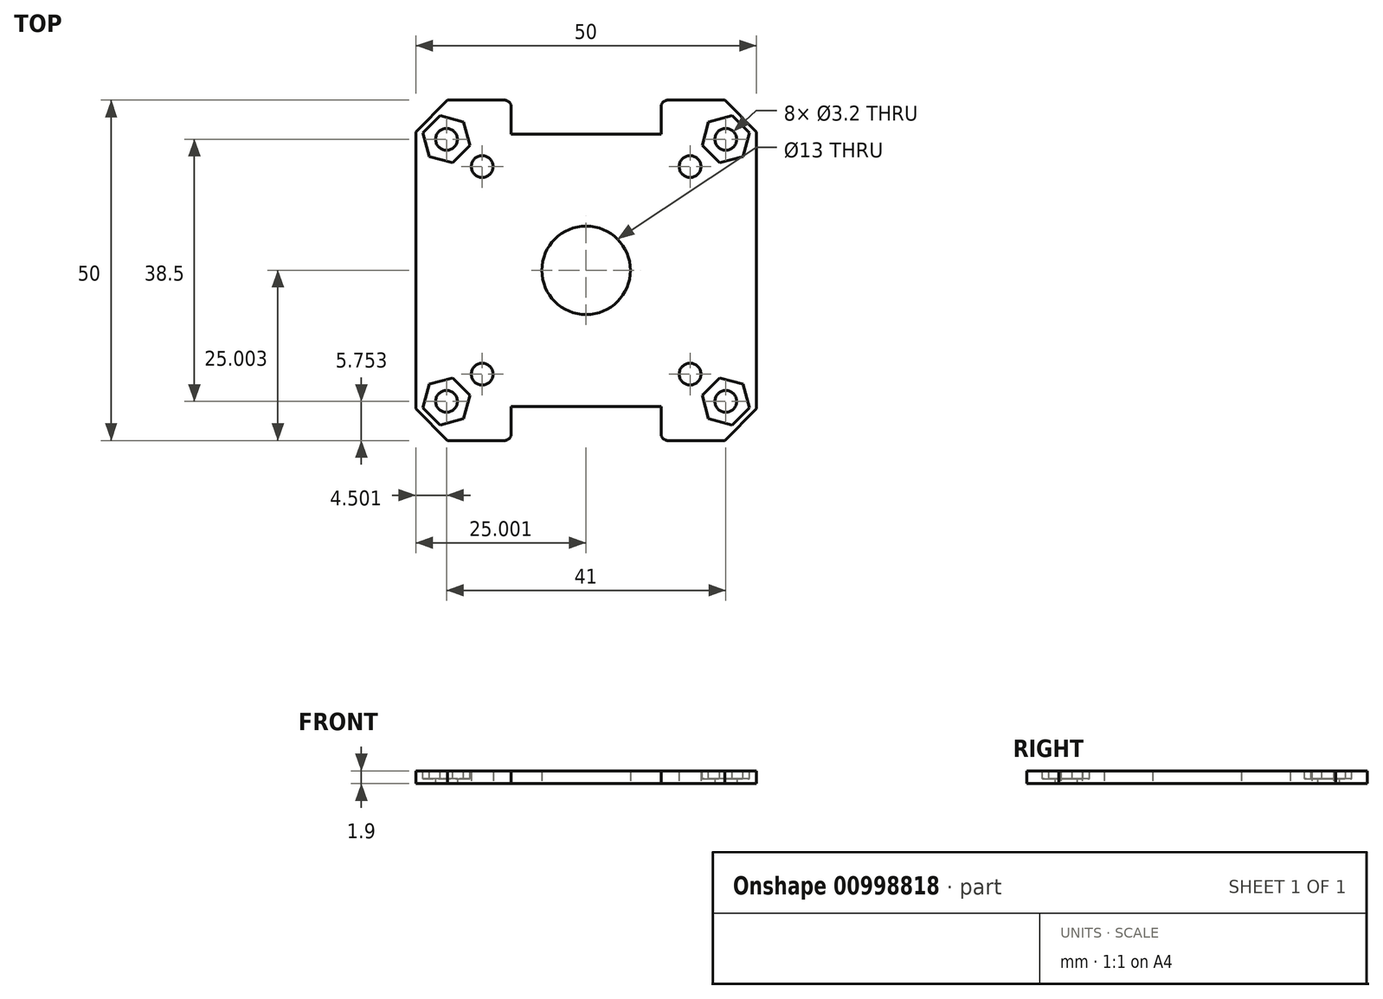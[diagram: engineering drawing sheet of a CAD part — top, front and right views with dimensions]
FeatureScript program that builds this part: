
annotation { "Feature Type Name" : "Feature", "Feature Type Description" : "" }
export const myFeature = defineFeature(function(context is Context, id is Id, definition is map)
    precondition{}
    {
        {
            var Q0;
            Q0=qCreatedBy(makeId("Top.planeOp"),FACE);
            var sketch = newSketch(context, id + "F0", { "sketchPlane" : qUnion([Q0])});
            skLineSegment(sketch, "E0.bottom", {"start": v(-29.7, 24.31) * mm, "end": v(11.3, 24.31) * mm, "construction": true});
            skLineSegment(sketch, "E0.top", {"start": v(-29.7, -14.19) * mm, "end": v(11.3, -14.19) * mm, "construction": true});
            skLineSegment(sketch, "E0.left", {"start": v(-29.7, 24.31) * mm, "end": v(-29.7, -14.19) * mm, "construction": true});
            skLineSegment(sketch, "E0.right", {"start": v(11.3, 24.31) * mm, "end": v(11.3, -14.19) * mm, "construction": true});
            skLineSegment(sketch, "E1", {"start": v(-29.7, 5.06) * mm, "end": v(11.3, 5.06) * mm, "construction": true});
            skCircle(sketch, "E2", {"center": v(-29.7, 24.31) * mm, "radius": 1.6 * mm});
            skCircle(sketch, "E3", {"center": v(11.3, 24.31) * mm, "radius": 1.6 * mm});
            skCircle(sketch, "E4", {"center": v(11.3, -14.19) * mm, "radius": 1.6 * mm});
            skCircle(sketch, "E5", {"center": v(-29.7, -14.19) * mm, "radius": 1.6 * mm});
            skLineSegment(sketch, "E6", {"start": v(-9.2, 24.31) * mm, "end": v(-9.2, -14.19) * mm, "construction": true});
            skPoint(sketch, "E7", {"position": v(-9.2, 5.06) * mm});
            skLineSegment(sketch, "E8.bottom", {"start": v(11.12, 30.06) * mm, "end": v(2.8, 30.06) * mm});
            skLineSegment(sketch, "E8.top", {"start": v(11.12, -19.94) * mm, "end": v(2.8, -19.94) * mm});
            skLineSegment(sketch, "E8.left", {"start": v(15.8, 25.4) * mm, "end": v(15.8, -15.27) * mm});
            skLineSegment(sketch, "E8.right", {"start": v(-34.2, 25.4) * mm, "end": v(-34.2, -15.27) * mm});
            skLineSegment(sketch, "E9.bottom", {"start": v(6.04, -10.19) * mm, "end": v(-24.46, -10.19) * mm, "construction": true});
            skLineSegment(sketch, "E9.top", {"start": v(6.04, 20.31) * mm, "end": v(-24.46, 20.31) * mm, "construction": true});
            skLineSegment(sketch, "E9.left", {"start": v(6.04, -10.19) * mm, "end": v(6.04, 20.31) * mm, "construction": true});
            skLineSegment(sketch, "E9.right", {"start": v(-24.46, -10.19) * mm, "end": v(-24.46, 20.31) * mm, "construction": true});
            skCircle(sketch, "E10", {"center": v(-24.46, 20.31) * mm, "radius": 1.6 * mm});
            skCircle(sketch, "E11", {"center": v(6.04, 20.31) * mm, "radius": 1.6 * mm});
            skCircle(sketch, "E12", {"center": v(6.04, -10.19) * mm, "radius": 1.6 * mm});
            skCircle(sketch, "E13", {"center": v(-24.46, -10.19) * mm, "radius": 1.6 * mm});
            skPoint(sketch, "E14.visualSharp", {"position": v(-34.2, 30.06) * mm});
            skPoint(sketch, "E15.visualSharp", {"position": v(15.8, 30.06) * mm});
            skPoint(sketch, "E16.visualSharp", {"position": v(15.8, -19.94) * mm});
            skPoint(sketch, "E17.visualSharp", {"position": v(-34.2, -19.94) * mm});
            skLineSegment(sketch, "E18.bottom", {"start": v(1.8, 25.06) * mm, "end": v(-20.2, 25.06) * mm});
            skLineSegment(sketch, "E18.top", {"start": v(1.8, -14.94) * mm, "end": v(-20.2, -14.94) * mm});
            skLineSegment(sketch, "E18.left", {"start": v(1.8, 25.06) * mm, "end": v(1.8, -14.94) * mm, "construction": true});
            skLineSegment(sketch, "E18.right", {"start": v(-20.2, 25.06) * mm, "end": v(-20.2, -14.94) * mm, "construction": true});
            skLineSegment(sketch, "E19", {"start": v(-20.2, 25.06) * mm, "end": v(-20.2, 29.06) * mm});
            skLineSegment(sketch, "E20", {"start": v(1.8, 25.06) * mm, "end": v(1.8, 29.06) * mm});
            skLineSegment(sketch, "E21", {"start": v(1.8, -14.94) * mm, "end": v(1.8, -18.94) * mm});
            skLineSegment(sketch, "E22", {"start": v(-20.2, -14.94) * mm, "end": v(-20.2, -18.94) * mm});
            skLineSegment(sketch, "E23.trimOffspring", {"start": v(-21.2, 30.06) * mm, "end": v(-29.54, 30.06) * mm});
            skLineSegment(sketch, "E24.trimOffspring", {"start": v(-21.2, -19.94) * mm, "end": v(-29.54, -19.94) * mm});
            skPoint(sketch, "E25.visualSharp", {"position": v(-20.2, 30.06) * mm});
            skArc(sketch, "E25.filletArc", {"start": v(-20.2, 29.06) * mm, "mid": v(-20.5, 29.77) * mm, "end": v(-21.2, 30.06) * mm});
            skPoint(sketch, "E26.visualSharp", {"position": v(1.8, 30.06) * mm});
            skArc(sketch, "E26.filletArc", {"start": v(2.8, 30.06) * mm, "mid": v(2.08, 29.77) * mm, "end": v(1.8, 29.06) * mm});
            skPoint(sketch, "E27.visualSharp", {"position": v(1.8, -19.94) * mm});
            skArc(sketch, "E27.filletArc", {"start": v(1.8, -18.94) * mm, "mid": v(2.08, -19.64) * mm, "end": v(2.8, -19.94) * mm});
            skPoint(sketch, "E28.visualSharp", {"position": v(-20.2, -19.94) * mm});
            skArc(sketch, "E28.filletArc", {"start": v(-21.2, -19.94) * mm, "mid": v(-20.5, -19.64) * mm, "end": v(-20.2, -18.94) * mm});
            skLineSegment(sketch, "E29", {"start": v(-29.54, 30.06) * mm, "end": v(-34.2, 25.4) * mm});
            skLineSegment(sketch, "E30", {"start": v(11.12, 30.06) * mm, "end": v(15.8, 25.4) * mm});
            skLineSegment(sketch, "E31", {"start": v(15.8, -15.27) * mm, "end": v(11.12, -19.94) * mm});
            skLineSegment(sketch, "E32", {"start": v(-29.54, -19.94) * mm, "end": v(-34.2, -15.27) * mm});
            skCircle(sketch, "E33", {"center": v(-9.2, 5.06) * mm, "radius": 6.5 * mm});
            skSolve(sketch);
        }
        {
            var Q0;
            Q0=makeQuery(id+"F0.imprint","IMPRINT",FACE,{"disambiguationData":[TD([[makeQuery(id+"F0.imprint","IMPRINT",EDGE,{"derivedFrom":sQuery(id+"F0.wireOp",EDGE,"E2")}),-1.0]])]});
            extrude(context, id + "F1", {"entities" : qUnion([Q0]), "depth" : 1.9 * mm, "offsetDistance" : 25 * mm});
        }
        {
            var Q0;
            Q0=makeQuery(id+"F1.opExtrude","CAP_FACE",FACE,{"disambiguationData":[OSD([sQuery(id+"F0.wireOp",EDGE,"E2"),sQuery(id+"F0.wireOp",EDGE,"E3"),sQuery(id+"F0.wireOp",EDGE,"E4"),sQuery(id+"F0.wireOp",EDGE,"E5"),sQuery(id+"F0.wireOp",EDGE,"E8.bottom"),sQuery(id+"F0.wireOp",EDGE,"E8.top"),sQuery(id+"F0.wireOp",EDGE,"E8.left"),sQuery(id+"F0.wireOp",EDGE,"E8.right"),sQuery(id+"F0.wireOp",EDGE,"E10"),sQuery(id+"F0.wireOp",EDGE,"E11"),sQuery(id+"F0.wireOp",EDGE,"E12"),sQuery(id+"F0.wireOp",EDGE,"E13"),sQuery(id+"F0.wireOp",EDGE,"E18.bottom"),sQuery(id+"F0.wireOp",EDGE,"E18.top"),sQuery(id+"F0.wireOp",EDGE,"E19"),sQuery(id+"F0.wireOp",EDGE,"E20"),sQuery(id+"F0.wireOp",EDGE,"E21"),sQuery(id+"F0.wireOp",EDGE,"E22"),sQuery(id+"F0.wireOp",EDGE,"E23.trimOffspring"),sQuery(id+"F0.wireOp",EDGE,"E24.trimOffspring"),sQuery(id+"F0.wireOp",EDGE,"E25.filletArc"),sQuery(id+"F0.wireOp",EDGE,"E26.filletArc"),sQuery(id+"F0.wireOp",EDGE,"E27.filletArc"),sQuery(id+"F0.wireOp",EDGE,"E28.filletArc"),sQuery(id+"F0.wireOp",EDGE,"E29"),sQuery(id+"F0.wireOp",EDGE,"E30"),sQuery(id+"F0.wireOp",EDGE,"E31"),sQuery(id+"F0.wireOp",EDGE,"E32"),sQuery(id+"F0.wireOp",EDGE,"E33")])],"isStart":false});
            var sketch = newSketch(context, id + "F2", { "sketchPlane" : qUnion([Q0])});
            skCircle(sketch, "E34.0", {"center": v(-29.7, 24.31) * mm, "radius": 1.6 * mm});
            skCircle(sketch, "E34.1", {"center": v(-24.46, 20.31) * mm, "radius": 1.6 * mm});
            skCircle(sketch, "E34.2", {"center": v(-9.2, 5.06) * mm, "radius": 6.5 * mm});
            skCircle(sketch, "E34.3", {"center": v(6.04, 20.31) * mm, "radius": 1.6 * mm});
            skCircle(sketch, "E34.4", {"center": v(11.3, 24.31) * mm, "radius": 1.6 * mm});
            skCircle(sketch, "E34.5", {"center": v(6.04, -10.19) * mm, "radius": 1.6 * mm});
            skCircle(sketch, "E34.6", {"center": v(11.3, -14.19) * mm, "radius": 1.6 * mm});
            skCircle(sketch, "E34.7", {"center": v(-24.46, -10.19) * mm, "radius": 1.6 * mm});
            skCircle(sketch, "E34.8", {"center": v(-29.7, -14.19) * mm, "radius": 1.6 * mm});
            skLineSegment(sketch, "E35", {"start": v(-24.46, -10.19) * mm, "end": v(6.04, 20.31) * mm, "construction": true});
            skLineSegment(sketch, "E36", {"start": v(-24.46, 20.31) * mm, "end": v(6.04, -10.19) * mm, "construction": true});
            skCircle(sketch, "E37.cCircle", {"center": v(-29.7, 24.31) * mm, "radius": 3.1 * mm, "construction": true});
            skLineSegment(sketch, "E37.0", {"start": v(-33.17, 25.24) * mm, "end": v(-30.64, 27.77) * mm});
            skLineSegment(sketch, "E37.1", {"start": v(-30.64, 27.77) * mm, "end": v(-27.18, 26.84) * mm});
            skLineSegment(sketch, "E37.2", {"start": v(-27.18, 26.84) * mm, "end": v(-26.25, 23.39) * mm});
            skLineSegment(sketch, "E37.3", {"start": v(-26.25, 23.39) * mm, "end": v(-28.78, 20.85) * mm});
            skLineSegment(sketch, "E37.4", {"start": v(-28.78, 20.85) * mm, "end": v(-32.24, 21.78) * mm});
            skLineSegment(sketch, "E37.5", {"start": v(-32.24, 21.78) * mm, "end": v(-33.17, 25.24) * mm});
            skPoint(sketch, "E37.0.midPoint", {"position": v(-31.9, 26.5) * mm});
            skCircle(sketch, "E38.cCircle", {"center": v(11.3, 24.31) * mm, "radius": 3.1 * mm, "construction": true});
            skLineSegment(sketch, "E38.0", {"start": v(12.22, 27.77) * mm, "end": v(14.75, 25.24) * mm});
            skLineSegment(sketch, "E38.1", {"start": v(14.75, 25.24) * mm, "end": v(13.82, 21.78) * mm});
            skLineSegment(sketch, "E38.2", {"start": v(13.82, 21.78) * mm, "end": v(10.36, 20.85) * mm});
            skLineSegment(sketch, "E38.3", {"start": v(10.36, 20.85) * mm, "end": v(7.83, 23.39) * mm});
            skLineSegment(sketch, "E38.4", {"start": v(7.83, 23.39) * mm, "end": v(8.76, 26.84) * mm});
            skLineSegment(sketch, "E38.5", {"start": v(8.76, 26.84) * mm, "end": v(12.22, 27.77) * mm});
            skPoint(sketch, "E38.0.midPoint", {"position": v(13.48, 26.5) * mm});
            skCircle(sketch, "E39.cCircle", {"center": v(11.3, -14.19) * mm, "radius": 3.1 * mm, "construction": true});
            skLineSegment(sketch, "E39.0", {"start": v(14.75, -15.11) * mm, "end": v(12.22, -17.65) * mm});
            skLineSegment(sketch, "E39.1", {"start": v(12.22, -17.65) * mm, "end": v(8.76, -16.72) * mm});
            skLineSegment(sketch, "E39.2", {"start": v(8.76, -16.72) * mm, "end": v(7.83, -13.26) * mm});
            skLineSegment(sketch, "E39.3", {"start": v(7.83, -13.26) * mm, "end": v(10.36, -10.73) * mm});
            skLineSegment(sketch, "E39.4", {"start": v(10.36, -10.73) * mm, "end": v(13.82, -11.66) * mm});
            skLineSegment(sketch, "E39.5", {"start": v(13.82, -11.66) * mm, "end": v(14.75, -15.11) * mm});
            skPoint(sketch, "E39.0.midPoint", {"position": v(13.48, -16.38) * mm});
            skCircle(sketch, "E40.cCircle", {"center": v(-29.7, -14.19) * mm, "radius": 3.1 * mm, "construction": true});
            skLineSegment(sketch, "E40.0", {"start": v(-30.64, -17.65) * mm, "end": v(-33.17, -15.11) * mm});
            skLineSegment(sketch, "E40.1", {"start": v(-33.17, -15.11) * mm, "end": v(-32.24, -11.66) * mm});
            skLineSegment(sketch, "E40.2", {"start": v(-32.24, -11.66) * mm, "end": v(-28.78, -10.73) * mm});
            skLineSegment(sketch, "E40.3", {"start": v(-28.78, -10.73) * mm, "end": v(-26.25, -13.26) * mm});
            skLineSegment(sketch, "E40.4", {"start": v(-26.25, -13.26) * mm, "end": v(-27.18, -16.72) * mm});
            skLineSegment(sketch, "E40.5", {"start": v(-27.18, -16.72) * mm, "end": v(-30.64, -17.65) * mm});
            skPoint(sketch, "E40.0.midPoint", {"position": v(-31.9, -16.38) * mm});
            skSolve(sketch);
        }
        {
            var Q0;
            Q0=makeQuery(id+"F2.imprint","IMPRINT",FACE,{"disambiguationData":[TD([[makeQuery(id+"F2.imprint","IMPRINT",EDGE,{"derivedFrom":sQuery(id+"F2.wireOp",EDGE,"45a267cd-e79d-4bba-a4c8-a550470966fd.0")}),-1.0]])]});
            var Q1;
            Q1=makeQuery(id+"F2.imprint","IMPRINT",FACE,{"disambiguationData":[TD([[makeQuery(id+"F2.imprint","IMPRINT",EDGE,{"derivedFrom":sQuery(id+"F2.wireOp",EDGE,"45a267cd-e79d-4bba-a4c8-a550470966fd.3")}),-1.0]])]});
            var Q2;
            Q2=makeQuery(id+"F2.imprint","IMPRINT",FACE,{"disambiguationData":[TD([[makeQuery(id+"F2.imprint","IMPRINT",EDGE,{"derivedFrom":sQuery(id+"F2.wireOp",EDGE,"45a267cd-e79d-4bba-a4c8-a550470966fd.2")}),-1.0]])]});
            var Q3;
            Q3=makeQuery(id+"F2.imprint","IMPRINT",FACE,{"disambiguationData":[TD([[makeQuery(id+"F2.imprint","IMPRINT",EDGE,{"derivedFrom":sQuery(id+"F2.wireOp",EDGE,"45a267cd-e79d-4bba-a4c8-a550470966fd.1")}),-1.0]])]});
            var Q4;
            Q4=makeQuery(id+"F2.imprint","IMPRINT",FACE,{"disambiguationData":[TD([[makeQuery(id+"F2.imprint","IMPRINT",EDGE,{"derivedFrom":sQuery(id+"F2.wireOp",EDGE,"E34.0")}),-1.0]])]});
            var Q5;
            Q5=makeQuery(id+"F2.imprint","IMPRINT",FACE,{"disambiguationData":[TD([[makeQuery(id+"F2.imprint","IMPRINT",EDGE,{"derivedFrom":sQuery(id+"F2.wireOp",EDGE,"E34.4")}),-1.0]])]});
            var Q6;
            Q6=makeQuery(id+"F2.imprint","IMPRINT",FACE,{"disambiguationData":[TD([[makeQuery(id+"F2.imprint","IMPRINT",EDGE,{"derivedFrom":sQuery(id+"F2.wireOp",EDGE,"E34.6")}),-1.0]])]});
            var Q7;
            Q7=makeQuery(id+"F2.imprint","IMPRINT",FACE,{"disambiguationData":[TD([[makeQuery(id+"F2.imprint","IMPRINT",EDGE,{"derivedFrom":sQuery(id+"F2.wireOp",EDGE,"E34.8")}),-1.0]])]});
            extrude(context, id + "F3", {"entities" : qUnion([Q0, Q1, Q2, Q3, Q4, Q5, Q6, Q7]), "operationType" : NewBodyOperationType.REMOVE, "oppositeDirection" : true, "depth" : 1.2 * mm, "offsetDistance" : 25 * mm});
        }
    });
